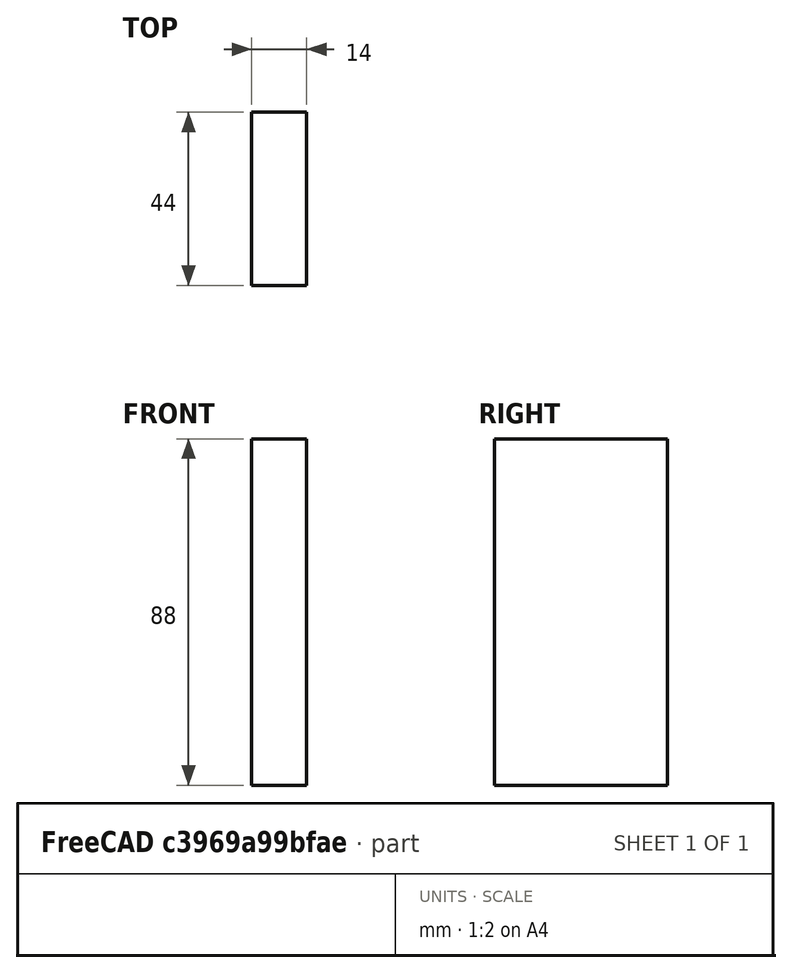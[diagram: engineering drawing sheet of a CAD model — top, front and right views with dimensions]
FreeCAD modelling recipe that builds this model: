
FCSTD DOCUMENT  (FreeCAD 0.19R24267 +99 (Git))
Label: test
License: All rights reserved
LicenseURL: http://en.wikipedia.org/wiki/All_rights_reserved
objects: Spreadsheet::Sheet×1, Sketcher::SketchObject×1, PartDesign::Pad×1, PartDesign::Body×1
note: 4 computed .brp shape members not serialized (recipe doc carries the construction recipe); baked Part::Feature solids carry a one-line shape summary decoded from their .brp

FEATURE [Spreadsheet::Sheet] Spreadsheet
  cells = A2=dim1; B2(dim1)=14; A3=dim2; B3(dim2)=44; A4=dim14; B4(dim14)=88; A5=dimm; B5(dimm)=77
FEATURE [Sketcher::SketchObject] Sketch
  FullyConstrained = true
  MapMode = 5
  Support = -> [XY_Plane]
  expr: Constraints[9] = <<Spreadsheet>>.dim2
  expr: Constraints[8] = <<Spreadsheet>>.dim1
  sketch-geometry (4):
    g0: LineSegment StartX=-7 StartY=22 StartZ=0 EndX=7 EndY=22 EndZ=0
    g1: LineSegment StartX=7 StartY=22 StartZ=0 EndX=7 EndY=-22 EndZ=0
    g2: LineSegment StartX=7 StartY=-22 StartZ=0 EndX=-7 EndY=-22 EndZ=0
    g3: LineSegment StartX=-7 StartY=-22 StartZ=0 EndX=-7 EndY=22 EndZ=0
  constraints (10):
    c: Coincident(g0,g1)
    c: Coincident(g1,g2)
    c: Coincident(g2,g3)
    c: Coincident(g3,g0)
    c: Horizontal(g2)
    c: Vertical(g3)
    c: Symmetric(g0,g0,g-2)
    c: Symmetric(g1,g0,g-1)
    c: DistanceX(g0,g0) = 14
    c: DistanceY(g3,g3) = 44
FEATURE [PartDesign::Pad] Pad
  Direction = (1,1,1)
  Length = 88
  Length2 = 100
  Profile = -> Sketch
  Refine = true
  Type = 0
  expr: Length = <<Spreadsheet>>.dim14
FEATURE [PartDesign::Body] Body
  Group = -> [Sketch,Pad]
  Origin = -> Origin
  Tip = -> Pad
